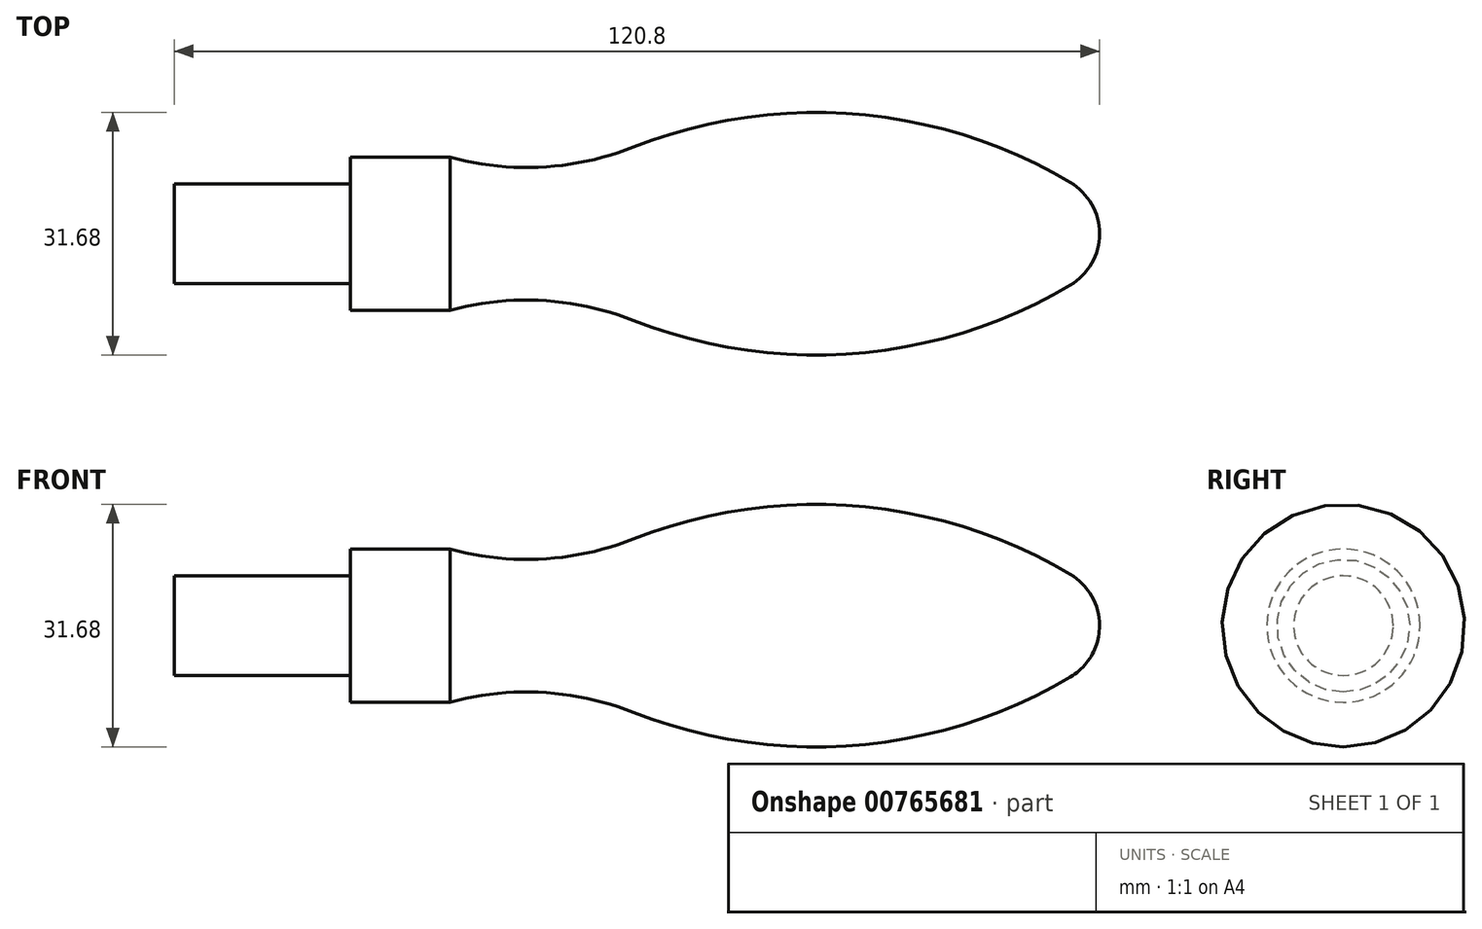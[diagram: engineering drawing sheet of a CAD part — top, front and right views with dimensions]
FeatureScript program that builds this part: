
annotation { "Feature Type Name" : "Feature", "Feature Type Description" : "" }
export const myFeature = defineFeature(function(context is Context, id is Id, definition is map)
    precondition{}
    {
        {
            var Q0;
            Q0=qCreatedBy(makeId("Front.planeOp"),FACE);
            var sketch = newSketch(context, id + "F0", { "sketchPlane" : qUnion([Q0])});
            skLineSegment(sketch, "E0", {"start": v(0, 0) * mm, "end": v(0, 6.5) * mm});
            skLineSegment(sketch, "E1", {"start": v(0, 6.5) * mm, "end": v(23, 6.5) * mm});
            skLineSegment(sketch, "E2", {"start": v(23, 6.5) * mm, "end": v(23, 10) * mm});
            skLineSegment(sketch, "E3", {"start": v(23, 10) * mm, "end": v(36, 10) * mm});
            skArc(sketch, "E4", {"start": v(36, 10) * mm, "mid": v(48.07, 8.72) * mm, "end": v(59.94, 11.3) * mm});
            skArc(sketch, "E5", {"start": v(116.99, 6.7) * mm, "mid": v(89, 15.63) * mm, "end": v(59.94, 11.3) * mm});
            skLineSegment(sketch, "E6", {"start": v(0, 0) * mm, "end": v(120.8, 0) * mm});
            skLineSegment(sketch, "E7", {"start": v(113, 8.9) * mm, "end": v(113, 7.8) * mm, "construction": true});
            skArc(sketch, "E8", {"start": v(120.8, 0) * mm, "mid": v(119.78, 3.86) * mm, "end": v(116.99, 6.7) * mm});
            skPoint(sketch, "E9.start.orphan", {"position": v(46, 30.94) * mm});
            skSolve(sketch);
        }
        {
            var Q0;
            Q0=makeQuery(id+"F0.imprint","IMPRINT",FACE,{"disambiguationData":[TD([[makeQuery(id+"F0.imprint","IMPRINT",EDGE,{"derivedFrom":sQuery(id+"F0.wireOp",EDGE,"E0")}),-1.0]])]});
            var Q1;
            Q1=sQuery(id+"F0.wireOp",EDGE,"E6");
            revolve(context, id + "F1", {"surfaceOperationType" : NewSurfaceOperationType.NEW, "entities" : qUnion([Q0]), "axis" : qUnion([Q1]), "revolveType" : RevolveType.ONE_DIRECTION, "oppositeDirection" : true, "angle" : 360 * degree});
        }
    });
